# Revit family: Sarlam_Lighting_Bulkhead_Chartres_Infini_T1_Vandal_resistant_Diam_322mm_2000Lm
name_source: partatom
category: Luminaires
units: mm (PartAtom-declared; Revit-internal decimal feet)

## family parameters
Cote de connecteur circulaire = Utiliser le diamètre
Couper avec des vides une fois chargée = Non
Hôte = Face
Partagée = Non
Point de calcul de pièce = Non
Source d'éclairage = Oui
Type d'élément = Normal

## types (14) — shared parameters
Angle de l'inclinaison = 0.00°
Antivandale Formes 2-4-7 = Oui
Built-in width = 322 mm  [stored 1.05643 ft]
Colour rendering index CRI = 80-89
Colour temperature K MAX = 4000
Colour temperature K MIN = 4000
Effective luminous flux lm = 2000
Elévation par défaut = 2500 mm  [stored 8.2021 ft]
Emettre la visibilité des formes dans le rendu = Non
Emettre à partir du diamètre du cercle = 250 mm  [stored 0.82021 ft]
Fabricant = LEGRAND
Fichier de distribution photométrique = SL532018.ies
Filtre de couleur = 16777215
General Conditions of Use = https://export.legrand.com
Gradation des changements de température de couleur de lampe = <Aucun>
Height/depth = 70 mm  [stored 0.229659 ft]
Lamp holder = None
Lamp power at multiwatt = 21/39W
Lamp type = LED not exchangeable
Length = 322 mm  [stored 1.05643 ft]
Light sharing = Symmetric
Material housing = Plastique
Nominal voltage (Un) V MAX = 253
Nominal voltage (Un) V MIN = 207
Outer diameter = 322 mm  [stored 1.05643 ft]
Protection Class = II
Radiation angle = Open beam
Suitable for built-in mounting = Non
Suitable for ceiling mounting = Oui
Suitable for surface mounting = Oui
Suitable for suspended mounting = Non
Suitable for wall mounting = Oui
Type of control gear = LED operating device current-controlled
URL = http://www.legrandoc.com
Voltage type = AC
Width = 322 mm  [stored 1.05643 ft]
zero-valued in all types: Built-in diameter, Built-in height/depth, Built-in length

## per-type parameters (varying)
| type | Colour housing | Degree of protection (IP) | Description | Detection area | Impact strength (IK) | Modèle | Nominal current mA MAX | Nominal current mA MIN | System power W | Type of dimming | With light sensor | With movement sensor |
| ON/OFF WHITE | LEGRAND - White | IP55 | CHARTRES INFINI 2000LM 4000K AV ON/OFF WHITE |  | IK10 | SL-532024 | 131 | 106 | 27 | Not regulable | Non | Non |
| ON/OFF ANTHRACITE | LEGRAND - Anthracite | IP55 | CHARTRES INFINI 2000LM 4000K AV ON/OFF BLACK |  | IK10 | SL-532025 | 131 | 106 | 27 | Not regulable | Non | Non |
| ON/OFF GREY METAL | LEGRAND - Grey | IP55 | CHARTRES INFINI 2000LM 4000K AV ON/OFF SLIVER |  | IK10 | SL-532026 | 131 | 106 | 27 | Not regulable | Non | Non |
| With microwave sensor WHITE | LEGRAND - White | IP55 | CHARTRES INFINI 2000LM 4000K  AV DETECTION HF WHITE | Detection at 2,5m high Ceiling: Ø6m max Wall: Ellipse 16*17m | IK10 | SL-532064 | 135 | 110 | 28 | Other | Oui | Oui |
| With microwave sensor ANTHRACITE | LEGRAND - Anthracite | IP55 | CHARTRES INFINI 2000LM 4000K  AV DETECTION HF BLACK | Detection at 2,5m high Ceiling: Ø6m max Wall: Ellipse 16*17m | IK10 | SL-532065 | 135 | 110 | 28 | Other | Oui | Oui |
| With microwave sensor GREY METAL | LEGRAND - Grey | IP55 | CHARTRES INFINI 2000LM 4000K  AV DETECTION HF SILVER | Detection at 2,5m high Ceiling: Ø6m max Wall: Ellipse 16*17m | IK10 | SL-532066 | 135 | 110 | 28 | Other | Oui | Oui |
| With microwave sensor + clock WHITE | LEGRAND - White | IP55 | CHARTRES INFINI 2000LM 4000K  AV DETECTION HF + CLOCK WHITE | Detection at 2,5m high Ceiling: Ø6m max Wall: Ellipse 16*17m | IK10 | SL-532079 | 135 | 110 | 28 | Other | Oui | Oui |
| With microwave sensor + clock ANTHRACITE | LEGRAND - Anthracite | IP55 | CHARTRES INFINI 2000LM 4000K  AV DETECTION HF + CLOCK BLACK | Detection at 2,5m high Ceiling: Ø6m max Wall: Ellipse 16*17m | IK10 | SL-532080 | 135 | 110 | 28 | Other | Oui | Oui |
| With microwave sensor + clock GREY METAL | LEGRAND - Grey | IP55 | CHARTRES INFINI 2000LM 4000K  AV DETECTION HF + CLOCK SLIVER | Detection at 2,5m high Ceiling: Ø6m max Wall: Ellipse 16*17m | IK10 | SL-532081 | 135 | 110 | 28 | Other | Oui | Oui |
| Double level / Timer WHITE | LEGRAND - White | IP55 | CHARTRES INFINI 2000LM 4000K AV BI-LEVEL/TIMER WHITE |  | IK10 | SL-532090 | 135 | 110 | 28 | Other | Non | Non |
| Double level / Timer ANTHRACITE | LEGRAND - Anthracite | IP55 | CHARTRES INFINI 2000LM 4000K  AV BI-LEVEL/TIMER BLACK |  | IK10 | SL-532091 | 135 | 110 | 28 | Other | Non | Non |
| Double level / Timer GREY METAL | LEGRAND - Grey | IP55 | CHARTRES INFINI 2000LM 4000K  AV BI-LEVEL/TIMER SLIVER |  | IK10 | SL-532092 | 135 | 110 | 28 | Other | Non | Non |
| Vandal resistant - ON/OFF | LEGRAND - White | IP66 | CHARTRES INFINI 2000LM 4000K SOLIROC ON/OFF WHITE |  | >IK10 | SL-532096 | 135 | 110 | 27 | Not regulable | Non | Non |
| Vandal resistant - With microwave sensor | LEGRAND - White | IP66 | CHARTRES INFINI 2000LM 4000K  SOLIROC DETECTION WHITE | Detection at 2,5m high Ceiling: Ø6m max Wall: Ellipse 16*17m | >IK10 | SL-532097 | 135 | 110 | 28 | Other | Oui | Oui |

note: [stored X ft] marks values corroborated as IEEE doubles in the binary element streams (Revit-internal decimal feet)

## geometry (parser evidence)
native form markers: Blend x10
no freeform markers — native parametric forms only
